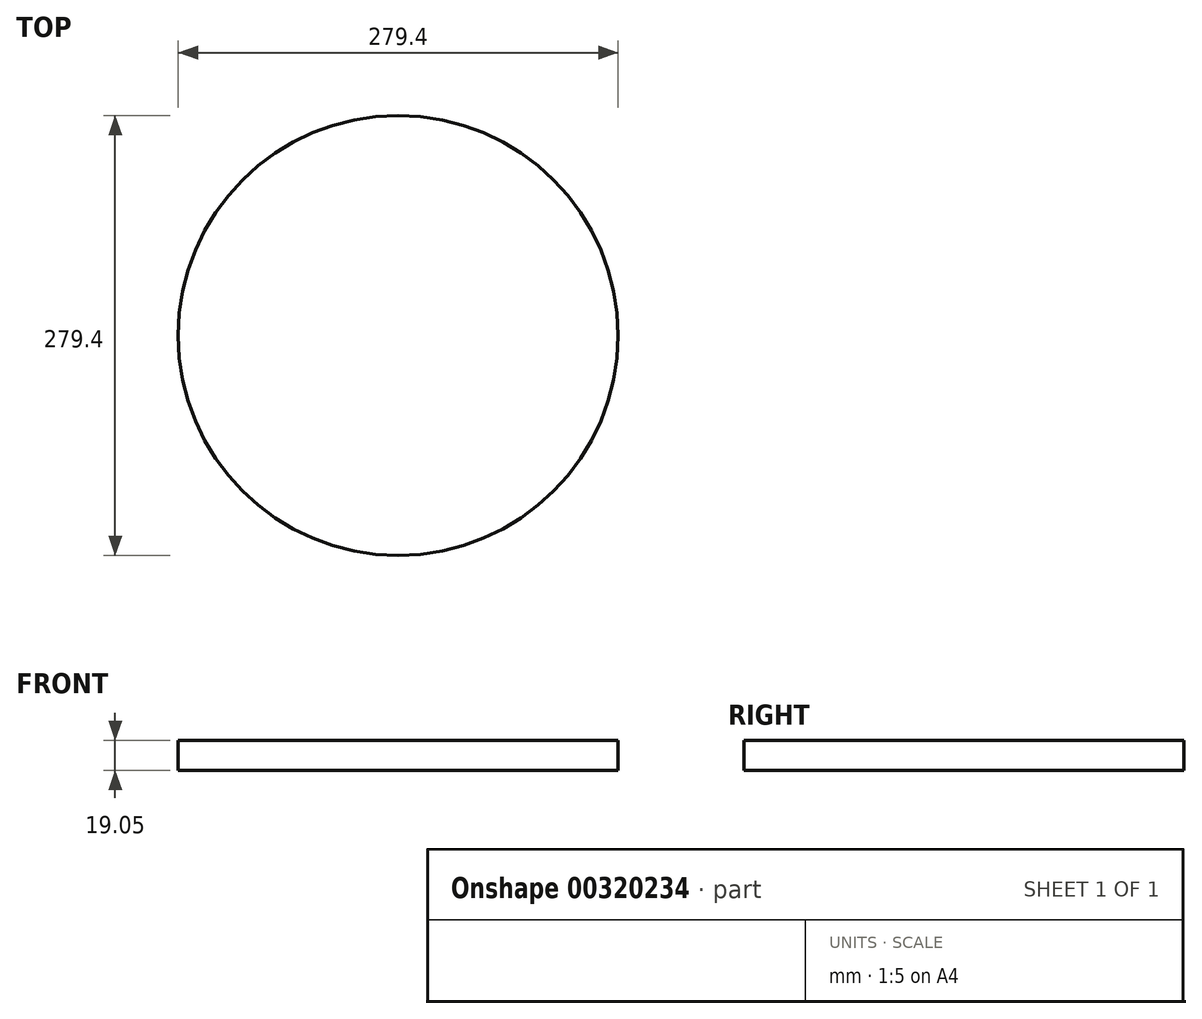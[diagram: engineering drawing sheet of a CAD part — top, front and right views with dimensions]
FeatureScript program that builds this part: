
annotation { "Feature Type Name" : "Feature", "Feature Type Description" : "" }
export const myFeature = defineFeature(function(context is Context, id is Id, definition is map)
    precondition{}
    {
        {
            var Q0;
            Q0=qCreatedBy(makeId("Top.planeOp"),FACE);
            var sketch = newSketch(context, id + "F0", { "sketchPlane" : qUnion([Q0])});
            skCircle(sketch, "E0", {"center": v(0, 0) * mm, "radius": 107.95 * mm, "construction": true});
            skCircle(sketch, "E1", {"center": v(0, 0) * mm, "radius": 139.7 * mm});
            skLineSegment(sketch, "E2", {"start": v(0, 0) * mm, "end": v(139.7, 0) * mm, "construction": true});
            skLineSegment(sketch, "E3", {"start": v(0, 0) * mm, "end": v(0, 139.7) * mm, "construction": true});
            skLineSegment(sketch, "E4", {"start": v(0, 0) * mm, "end": v(76.33, 76.33) * mm, "construction": true});
            skLineSegment(sketch, "E5", {"start": v(0, 0) * mm, "end": v(101.44, 36.92) * mm, "construction": true});
            skLineSegment(sketch, "E6", {"start": v(0, 0) * mm, "end": v(36.92, 101.44) * mm, "construction": true});
            skCircle(sketch, "E7", {"center": v(36.92, 101.44) * mm, "radius": 17.46 * mm});
            skCircle(sketch, "E8", {"center": v(76.33, 76.33) * mm, "radius": 17.46 * mm});
            skCircle(sketch, "E9", {"center": v(101.44, 36.92) * mm, "radius": 17.46 * mm});
            skLineSegment(sketch, "E10.top", {"start": v(-9.53, 113.97) * mm, "end": v(9.52, 113.97) * mm});
            skLineSegment(sketch, "E10.left", {"start": v(-9.53, 139.37) * mm, "end": v(-9.53, 113.97) * mm});
            skLineSegment(sketch, "E10.right", {"start": v(9.52, 139.37) * mm, "end": v(9.52, 113.97) * mm});
            skPoint(sketch, "E10.middle", {"position": v(0, 126.67) * mm});
            skLineSegment(sketch, "E11", {"start": v(-9.53, 120.32) * mm, "end": v(9.52, 120.32) * mm});
            skSolve(sketch);
        }
        {
            var Q0;
            Q0=qSketchRegion(id+"F0",true);
            var Q1;
            Q1=makeQuery(id+"F0.imprint","IMPRINT",FACE,{"disambiguationData":[TD([[makeQuery(id+"F0.imprint","IMPRINT",EDGE,{"derivedFrom":sQuery(id+"F0.wireOp",EDGE,"E7")}),1.0]])]});
            var Q2;
            Q2=makeQuery(id+"F0.imprint","IMPRINT",FACE,{"disambiguationData":[TD([[makeQuery(id+"F0.imprint","IMPRINT",EDGE,{"derivedFrom":sQuery(id+"F0.wireOp",EDGE,"E8")}),1.0]])]});
            var Q3;
            Q3=makeQuery(id+"F0.imprint","IMPRINT",FACE,{"disambiguationData":[TD([[makeQuery(id+"F0.imprint","IMPRINT",EDGE,{"derivedFrom":sQuery(id+"F0.wireOp",EDGE,"E9")}),1.0]])]});
            var Q4;
            {var subQ0=sQuery(id+"F0.wireOp",EDGE,"E10.top");Q4=makeQuery(id+"F0.imprint","IMPRINT",FACE,{"disambiguationData":[TD([[makeQuery(id+"F0.imprint","IMPRINT",EDGE,{"derivedFrom":subQ0}),1.0]])]});}
            extrude(context, id + "F1", {"entities" : qUnion([Q0, Q1, Q2, Q3, Q4]), "oppositeDirection" : true, "depth" : 19.05 * mm});
        }
        {
            var Q0;
            Q0=qCreatedBy(makeId("Front.planeOp"),FACE);
            var sketch = newSketch(context, id + "F2", { "sketchPlane" : qUnion([Q0])});
            skLineSegment(sketch, "E12", {"start": v(0, 0) * mm, "end": v(0, 89.72) * mm, "construction": true});
            skSolve(sketch);
        }
    });
